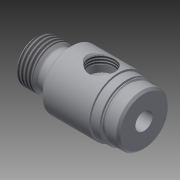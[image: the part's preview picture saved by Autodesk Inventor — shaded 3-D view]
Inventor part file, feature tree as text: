
AUTODESK INVENTOR PART (.ipt)
format: ipt  version: 2014 SP2 (Build 180246200, 246)  size: 275,968 bytes
history: native  units: in
note: dims shown in document units (in); Inventor stores cm internally (conversion verified against a paired STEP export)
features: other x119, sketch x6, revolve x5, thread x2, hole x1
ambient origin geometry x8: Origin, YZ Plane, XZ Plane, XY Plane, X Axis, Y Axis, Z Axis, Center Point
bodies: Solid1 (feature_tree)
feature tree (133):
  revolve  "Revolution1"  [1 undecoded]
  thread  "Thread1"  [1 undecoded]
  revolve  "Revolution2"  Angle=360.0deg
  hole  "Hole1"  [1 undecoded]
  revolve  "Revolution3"  [1 undecoded]
  revolve  "Revolution4"  [1 undecoded]
  thread  "Thread2"  [1 undecoded]
  revolve  "Revolution5"  [1 undecoded]
  other  "dp1_XY"
  other  "dp1_YZ"
  other  "dp1_ZX"
  other  "dp1_X"
  other  "dp1_Y"
  other  "dp1_Z"
  other  "dp1_Center"
  other  "dp2_XY"
  other  "dp2_YZ"
  other  "dp2_ZX"
  other  "dp2_X"
  other  "dp2_Y"
  other  "dp2_Z"
  other  "dp2_Center"
  other  "hh_XY"
  other  "hh_YZ"
  other  "hh_ZX"
  other  "hh_X"
  other  "hh_Y"
  other  "hh_Z"
  other  "hh_Center"
  other  "port_XY"
  other  "port_YZ"
  other  "port_ZX"
  other  "port_X"
  other  "port_Y"
  other  "port_Z"
  other  "port_Center"
  other  "rod_guide_XY"
  other  "rod_guide_YZ"
  other  "rod_guide_ZX"
  other  "rod_guide_X"
  other  "rod_guide_Y"
  other  "rod_guide_Z"
  other  "rod_guide_Center"
  other  "s1_XY"
  other  "s1_YZ"
  other  "s1_ZX"
  other  "s1_X"
  other  "s1_Y"
  other  "s1_Z"
  other  "s1_Center"
  other  "s2_XY"
  other  "s2_YZ"
  other  "s2_ZX"
  other  "s2_X"
  other  "s2_Y"
  other  "s2_Z"
  other  "s2_Center"
  other  "t1_XY"
  other  "t1_YZ"
  other  "t1_ZX"
  other  "t1_X"
  other  "t1_Y"
  other  "t1_Z"
  other  "t1_Center"
  other  "t111_XY"
  other  "t111_YZ"
  other  "t111_ZX"
  other  "t111_X"
  other  "t111_Y"
  other  "t111_Z"
  other  "t111_Center"
  other  "to_foot_bracket_XY"
  other  "to_foot_bracket_YZ"
  other  "to_foot_bracket_ZX"
  other  "to_foot_bracket_X"
  other  "to_foot_bracket_Y"
  other  "to_foot_bracket_Z"
  other  "to_foot_bracket_Center"
  other  "to_nut_XY"
  other  "to_nut_YZ"
  other  "to_nut_ZX"
  other  "to_nut_X"
  other  "to_nut_Y"
  other  "to_nut_Z"
  other  "to_nut_Center"
  other  "to_rod_XY"
  other  "to_rod_YZ"
  other  "to_rod_ZX"
  other  "to_rod_X"
  other  "to_rod_Y"
  other  "to_rod_Z"
  other  "to_rod_Center"
  other  "to_screw_XY"
  other  "to_screw_YZ"
  other  "to_screw_ZX"
  other  "to_screw_X"
  other  "to_screw_Y"
  other  "to_screw_Z"
  other  "to_screw_Center"
  other  "to_trunnion_brackets_XY"
  other  "to_trunnion_brackets_YZ"
  other  "to_trunnion_brackets_ZX"
  other  "to_trunnion_brackets_X"
  other  "to_trunnion_brackets_Y"
  other  "to_trunnion_brackets_Z"
  other  "to_trunnion_brackets_Center"
  other  "to_trunnion_brackets1_XY"
  other  "to_trunnion_brackets1_YZ"
  other  "to_trunnion_brackets1_ZX"
  other  "to_trunnion_brackets1_X"
  other  "to_trunnion_brackets1_Y"
  other  "to_trunnion_brackets1_Z"
  other  "to_trunnion_brackets1_Center"
  other  "to_trunnion_brackets2_XY"
  other  "to_trunnion_brackets2_YZ"
  other  "to_trunnion_brackets2_ZX"
  other  "to_trunnion_brackets2_X"
  other  "to_trunnion_brackets2_Y"
  other  "to_trunnion_brackets2_Z"
  other  "to_trunnion_brackets2_Center"
  other  "to_tube_XY"
  other  "to_tube_YZ"
  other  "to_tube_ZX"
  other  "to_tube_X"
  other  "to_tube_Y"
  other  "to_tube_Z"
  other  "to_tube_Center"
  sketch  "Sketch_2"  dims[d0=360.0deg d1=0.23in d2=0.0in d3=360.0deg]
  sketch  "Sketch_3"  dims[d4=0.2535in d5=0.75in d6=0.2735in d7=0.25in d8=90.0deg d9=1.594in d10=0.0in d11=360.0deg]
  sketch  "Sketch3"  dims[d12=360.0deg d13=0.1251in d14=0.0in]
  sketch  "Sketch_10"  dims[d15=360.0deg]
  sketch  "Sketch_43"  dims[d16=0.0in d17=0.0in d18=0.0in d19=0.0in d20=0.0in d21=0.0in]
  sketch  "Sketch_47"
note: 7 required parameter values undecoded (feature->parameter linkage not recoverable at this tier; creation-order binding heuristic only, values carry confidence <= 0.55)